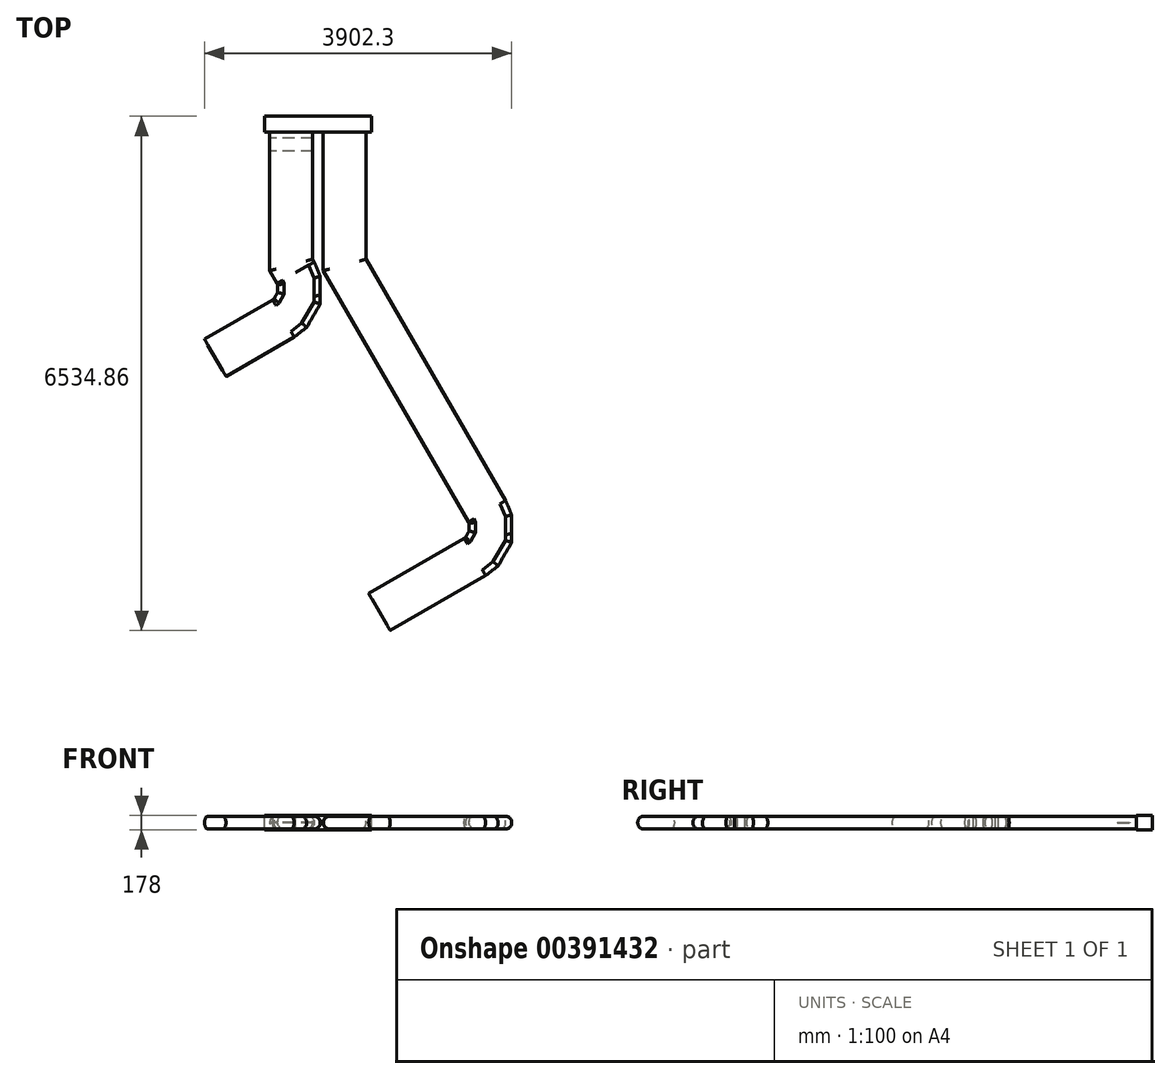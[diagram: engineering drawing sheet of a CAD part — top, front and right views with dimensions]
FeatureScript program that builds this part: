
annotation { "Feature Type Name" : "Feature", "Feature Type Description" : "" }
export const myFeature = defineFeature(function(context is Context, id is Id, definition is map)
    precondition{}
    {
        {
            var Q0;
            Q0=qCreatedBy(makeId("Front.planeOp"),FACE);
            var sketch = newSketch(context, id + "F0", { "sketchPlane" : qUnion([Q0])});
            skLineSegment(sketch, "E0.bottom", {"start": v(680, -89) * mm, "end": v(-680, -89) * mm});
            skLineSegment(sketch, "E0.top", {"start": v(680, 89) * mm, "end": v(-680, 89) * mm});
            skLineSegment(sketch, "E0.left", {"start": v(680, -89) * mm, "end": v(680, 89) * mm});
            skLineSegment(sketch, "E0.right", {"start": v(-680, -89) * mm, "end": v(-680, 89) * mm});
            skPoint(sketch, "E0.middle", {"position": v(0, 0) * mm});
            skSolve(sketch);
        }
        {
            var Q0;
            Q0=qSketchRegion(id+"F0",true);
            extrude(context, id + "F1", {"entities" : qUnion([Q0]), "depth" : 200 * mm});
        }
        {
            var Q0;
            Q0=makeQuery(id+"F1.opExtrude","CAP_FACE",FACE,{"disambiguationData":[OSD([sQuery(id+"F0.wireOp",EDGE,"E0.bottom"),sQuery(id+"F0.wireOp",EDGE,"E0.top"),sQuery(id+"F0.wireOp",EDGE,"E0.left"),sQuery(id+"F0.wireOp",EDGE,"E0.right")])],"isStart":false});
            var sketch = newSketch(context, id + "F2", { "sketchPlane" : qUnion([Q0])});
            skLineSegment(sketch, "E1.bottom", {"start": v(-150, -82.5) * mm, "end": v(-530, -82.5) * mm});
            skLineSegment(sketch, "E1.top", {"start": v(-150, 82.5) * mm, "end": v(-530, 82.5) * mm});
            skPoint(sketch, "E1.middle", {"position": v(-340, 0) * mm});
            skArc(sketch, "E2", {"start": v(-530, 82.5) * mm, "mid": v(-612.5, 0) * mm, "end": v(-530, -82.5) * mm});
            skArc(sketch, "E3", {"start": v(-150, -82.5) * mm, "mid": v(-67.5, 0) * mm, "end": v(-150, 82.5) * mm});
            skLineSegment(sketch, "E4.MirrorCS", {"start": v(150, -82.5) * mm, "end": v(530, -82.5) * mm});
            skLineSegment(sketch, "E5.MirrorCS", {"start": v(150, 82.5) * mm, "end": v(530, 82.5) * mm});
            skArc(sketch, "E6.MirrorCS", {"start": v(150, -82.5) * mm, "mid": v(67.5, 0) * mm, "end": v(150, 82.5) * mm});
            skArc(sketch, "E7.MirrorCS", {"start": v(530, 82.5) * mm, "mid": v(612.5, 0) * mm, "end": v(530, -82.5) * mm});
            skSolve(sketch);
        }
        {
            var Q0;
            Q0=makeQuery(id+"F2.imprint","IMPRINT",FACE,{"disambiguationData":[TD([[makeQuery(id+"F2.imprint","IMPRINT",EDGE,{"derivedFrom":sQuery(id+"F2.wireOp",EDGE,"E1.bottom")}),-1.0]])]});
            var Q1;
            Q1=makeQuery(id+"F2.imprint","IMPRINT",FACE,{"disambiguationData":[TD([[makeQuery(id+"F2.imprint","IMPRINT",EDGE,{"derivedFrom":sQuery(id+"F2.wireOp",EDGE,"E4.MirrorCS")}),1.0]])]});
            extrude(context, id + "F3", {"entities" : qUnion([Q0, Q1]), "operationType" : NewBodyOperationType.ADD, "depth" : 50 * mm});
        }
        {
            var Q0;
            Q0=makeQuery(id+"F1.opExtrude","SWEPT_BODY",BODY,{"disambiguationData":[OSD([sQuery(id+"F0.wireOp",EDGE,"E0.bottom"),sQuery(id+"F0.wireOp",EDGE,"E0.top"),sQuery(id+"F0.wireOp",EDGE,"E0.left"),sQuery(id+"F0.wireOp",EDGE,"E0.right")])]});
            transform(context, id + "F4", {"entities" : qUnion([Q0]), "transformType" : TransformType.TRANSLATION_3D, "dx" : 0 * mm, "dy" : 0 * mm, "dz" : 0 * mm, "makeCopy" : true});
        }
        {
            var Q0;
            Q0=makeQuery(id+"F4.opPattern","COPY",BODY,{"derivedFrom":makeQuery(id+"F1.opExtrude","SWEPT_BODY",BODY,{"disambiguationData":[OSD([sQuery(id+"F0.wireOp",EDGE,"E0.bottom"),sQuery(id+"F0.wireOp",EDGE,"E0.top"),sQuery(id+"F0.wireOp",EDGE,"E0.left"),sQuery(id+"F0.wireOp",EDGE,"E0.right")])]}),"instanceName":"1"});
            deleteBodies(context, id + "F5", {"entities" : qUnion([Q0])});
        }
        {
            var Q0;
            Q0=makeQuery(id+"F1.opExtrude","SWEPT_BODY",BODY,{"disambiguationData":[OSD([sQuery(id+"F0.wireOp",EDGE,"E0.bottom"),sQuery(id+"F0.wireOp",EDGE,"E0.top"),sQuery(id+"F0.wireOp",EDGE,"E0.left"),sQuery(id+"F0.wireOp",EDGE,"E0.right")])]});
            transform(context, id + "F6", {"entities" : qUnion([Q0]), "transformType" : TransformType.COPY});
        }
        {
            var Q0;
            Q0=makeQuery(id+"F6.opPattern","COPY",BODY,{"derivedFrom":makeQuery(id+"F1.opExtrude","SWEPT_BODY",BODY,{"disambiguationData":[OSD([sQuery(id+"F0.wireOp",EDGE,"E0.bottom"),sQuery(id+"F0.wireOp",EDGE,"E0.top"),sQuery(id+"F0.wireOp",EDGE,"E0.left"),sQuery(id+"F0.wireOp",EDGE,"E0.right")])]}),"instanceName":"1"});
            transform(context, id + "F7", {"entities" : qUnion([Q0]), "transformType" : TransformType.TRANSLATION_3D, "dx" : 0 * mm, "dy" : 0 * mm, "dz" : 0 * mm, "makeCopy" : true});
        }
        {
            var Q0;
            Q0=makeQuery(id+"F7.opPattern","COPY",BODY,{"derivedFrom":makeQuery(id+"F6.opPattern","COPY",BODY,{"derivedFrom":makeQuery(id+"F1.opExtrude","SWEPT_BODY",BODY,{"disambiguationData":[OSD([sQuery(id+"F0.wireOp",EDGE,"E0.bottom"),sQuery(id+"F0.wireOp",EDGE,"E0.top"),sQuery(id+"F0.wireOp",EDGE,"E0.left"),sQuery(id+"F0.wireOp",EDGE,"E0.right")])]}),"instanceName":"1"}),"instanceName":"1"});
            deleteBodies(context, id + "F8", {"entities" : qUnion([Q0])});
        }
        {
            var Q0;
            Q0=makeQuery(id+"F6.opPattern","COPY",BODY,{"derivedFrom":makeQuery(id+"F1.opExtrude","SWEPT_BODY",BODY,{"disambiguationData":[OSD([sQuery(id+"F0.wireOp",EDGE,"E0.bottom"),sQuery(id+"F0.wireOp",EDGE,"E0.top"),sQuery(id+"F0.wireOp",EDGE,"E0.left"),sQuery(id+"F0.wireOp",EDGE,"E0.right")])]}),"instanceName":"1"});
            deleteBodies(context, id + "F9", {"entities" : qUnion([Q0])});
        }
        {
            var Q0;
            Q0=makeQuery(id+"F3.opExtrude","CAP_FACE",FACE,{"disambiguationData":[OSD([sQuery(id+"F2.wireOp",EDGE,"E1.bottom"),sQuery(id+"F2.wireOp",EDGE,"E1.top"),sQuery(id+"F2.wireOp",EDGE,"E2"),sQuery(id+"F2.wireOp",EDGE,"E3")])],"isStart":false});
            var sketch = newSketch(context, id + "F10", { "sketchPlane" : qUnion([Q0])});
            skSolve(sketch);
        }
        {
            var Q0;
            Q0=makeQuery(id+"F10.imprint","IMPRINT",FACE,{"disambiguationData":[TD([[makeQuery(id+"F10.imprint","IMPRINT",EDGE,{"derivedFrom":makeQuery(id+"F3.opExtrude","CAP_EDGE",EDGE,{"disambiguationData":[OSD([sQuery(id+"F2.wireOp",EDGE,"E1.bottom")])],"isStart":false})}),-1.0]])]});
            extrude(context, id + "F11", {"entities" : qUnion([Q0]), "operationType" : NewBodyOperationType.ADD, "depth" : 25 * mm});
        }
        {
            var Q0;
            Q0=makeQuery(id+"F11.opExtrude","CAP_FACE",FACE,{"disambiguationData":[OSD([sQuery(id+"F2.wireOp",EDGE,"E1.bottom"),sQuery(id+"F2.wireOp",EDGE,"E1.top"),sQuery(id+"F2.wireOp",EDGE,"E2"),sQuery(id+"F2.wireOp",EDGE,"E3")])],"isStart":false});
            var sketch = newSketch(context, id + "F12", { "sketchPlane" : qUnion([Q0])});
            skLineSegment(sketch, "E8", {"start": v(-67.5, 0) * mm, "end": v(-612.5, 0) * mm, "construction": true});
            skLineSegment(sketch, "E9", {"start": v(-340, 82.5) * mm, "end": v(-340, -82.5) * mm, "construction": true});
            skLineSegment(sketch, "E10.bottom", {"start": v(-530, 82.5) * mm, "end": v(-150, 82.5) * mm});
            skLineSegment(sketch, "E10.top", {"start": v(-530, -82.5) * mm, "end": v(-150, -82.5) * mm});
            skPoint(sketch, "E10.middle", {"position": v(-340, 0) * mm});
            skArc(sketch, "E11", {"start": v(-530, 82.5) * mm, "mid": v(-587.98, 58.69) * mm, "end": v(-612.5, 1) * mm});
            skArc(sketch, "E12", {"start": v(-150, -82.5) * mm, "mid": v(-67.5, 0) * mm, "end": v(-150, 82.5) * mm});
            skLineSegment(sketch, "E13.0", {"start": v(-67.5, 1) * mm, "end": v(-612.5, 1) * mm});
            skLineSegment(sketch, "E14.0", {"start": v(-67.5, -1) * mm, "end": v(-612.5, -1) * mm});
            skArc(sketch, "E15.trimOffspring", {"start": v(-612.5, 0) * mm, "mid": v(-588.34, -58.34) * mm, "end": v(-530, -82.5) * mm});
            skSolve(sketch);
        }
        {
            var Q0;
            {var subQ0=sQuery(id+"F12.wireOp",EDGE,"E10.top");Q0=makeQuery(id+"F12.imprint","IMPRINT",FACE,{"disambiguationData":[TD([[makeQuery(id+"F12.imprint","IMPRINT",EDGE,{"derivedFrom":subQ0}),-1.0]])]});}
            var Q1;
            {var subQ0=sQuery(id+"F12.wireOp",EDGE,"E10.bottom");Q1=makeQuery(id+"F12.imprint","IMPRINT",FACE,{"disambiguationData":[TD([[makeQuery(id+"F12.imprint","IMPRINT",EDGE,{"derivedFrom":subQ0}),1.0]])]});}
            extrude(context, id + "F13", {"entities" : qUnion([Q0, Q1]), "operationType" : NewBodyOperationType.ADD, "depth" : 165 * mm});
        }
        {
            var Q0;
            Q0=makeQuery(id+"F3.opExtrude","CAP_FACE",FACE,{"disambiguationData":[OSD([sQuery(id+"F2.wireOp",EDGE,"E4.MirrorCS"),sQuery(id+"F2.wireOp",EDGE,"E5.MirrorCS"),sQuery(id+"F2.wireOp",EDGE,"E6.MirrorCS"),sQuery(id+"F2.wireOp",EDGE,"E7.MirrorCS")])],"isStart":false});
            extrude(context, id + "F14", {"entities" : qUnion([Q0]), "operationType" : NewBodyOperationType.ADD, "depth" : 1500 * mm});
        }
        {
            var Q0;
            Q0=makeQuery(id+"F13.opExtrude","CAP_FACE",FACE,{"disambiguationData":[OSD([sQuery(id+"F12.wireOp",EDGE,"E10.bottom"),sQuery(id+"F12.wireOp",EDGE,"E11"),sQuery(id+"F12.wireOp",EDGE,"E12"),sQuery(id+"F12.wireOp",EDGE,"E13.0")])],"isStart":false});
            var sketch = newSketch(context, id + "F15", { "sketchPlane" : qUnion([Q0])});
            skLineSegment(sketch, "E16", {"start": v(-340, 1) * mm, "end": v(-340, -1) * mm, "construction": true});
            skLineSegment(sketch, "E17.bottom", {"start": v(-150, -82.5) * mm, "end": v(-530, -82.5) * mm});
            skLineSegment(sketch, "E17.top", {"start": v(-150, 82.5) * mm, "end": v(-530, 82.5) * mm});
            skPoint(sketch, "E17.middle", {"position": v(-340, 0) * mm});
            skArc(sketch, "E18", {"start": v(-530, 82.5) * mm, "mid": v(-612.5, 0) * mm, "end": v(-530, -82.5) * mm});
            skArc(sketch, "E19", {"start": v(-150, -82.5) * mm, "mid": v(-67.5, 0) * mm, "end": v(-150, 82.5) * mm});
            skSolve(sketch);
        }
        {
            var Q0;
            Q0 = qSketchRegion(id + "F15", true);
            extrude(context, id + "F16", {"entities" : qUnion([Q0]), "operationType" : NewBodyOperationType.ADD, "depth" : 1335 * mm});
        }
        {
            var Q0;
            Q0=makeQuery(id+"F14.opExtrude","CAP_FACE",FACE,{"disambiguationData":[OSD([sQuery(id+"F2.wireOp",EDGE,"E4.MirrorCS"),sQuery(id+"F2.wireOp",EDGE,"E5.MirrorCS"),sQuery(id+"F2.wireOp",EDGE,"E6.MirrorCS"),sQuery(id+"F2.wireOp",EDGE,"E7.MirrorCS")])],"isStart":false});
            extrude(context, id + "F17", {"entities" : qUnion([Q0]), "operationType" : NewBodyOperationType.ADD, "depth" : 25 * mm});
        }
        {
            var Q0;
            Q0=makeQuery(id+"F16.opExtrude","CAP_FACE",FACE,{"disambiguationData":[OSD([sQuery(id+"F15.wireOp",EDGE,"E17.bottom"),sQuery(id+"F15.wireOp",EDGE,"E17.top"),sQuery(id+"F15.wireOp",EDGE,"E18"),sQuery(id+"F15.wireOp",EDGE,"E19")])],"isStart":false});
            var sketch = newSketch(context, id + "F18", { "sketchPlane" : qUnion([Q0])});
            skPoint(sketch, "E20", {"position": v(-340, 0) * mm});
            skPoint(sketch, "E21.orphan", {"position": v(-340, 82.5) * mm});
            skPoint(sketch, "E22.end.orphan", {"position": v(-340, -82.5) * mm});
            skPoint(sketch, "E23.orphan", {"position": v(-67.5, 0) * mm});
            skPoint(sketch, "E24.start.orphan", {"position": v(-612.5, 0) * mm});
            skLineSegment(sketch, "E25", {"start": v(-612.5, 0) * mm, "end": v(-67.5, 0) * mm, "construction": true});
            skLineSegment(sketch, "E26", {"start": v(-340, 82.5) * mm, "end": v(-340, -82.5) * mm, "construction": true});
            skSolve(sketch);
        }
        {
            var Q0;
            Q0=sQuery(id+"F18.wireOp",EDGE,"E25");
            cPlane(context, id + "F19", {"entities" : qUnion([Q0]), "cplaneType" : CPlaneType.LINE_ANGLE, "offset" : 25 * mm, "angle" : 90 * degree, "width" : 150 * mm, "height" : 150 * mm});
        }
        {
            var Q0;
            Q0=makeQuery(id+"F18.imprint","IMPRINT",FACE,{"disambiguationData":[TD([[makeQuery(id+"F18.imprint","IMPRINT",EDGE,{"derivedFrom":makeQuery(id+"F16.opExtrude","CAP_EDGE",EDGE,{"disambiguationData":[OSD([sQuery(id+"F15.wireOp",EDGE,"E17.bottom")])],"isStart":false})}),-1.0]])]});
            var sketch = newSketch(context, id + "F20", { "sketchPlane" : qUnion([Q0])});
            skArc(sketch, "E27.0", {"start": v(-530, 82.5) * mm, "mid": v(-612.5, 0) * mm, "end": v(-530, -82.5) * mm});
            skArc(sketch, "E27.1", {"start": v(-150, -82.5) * mm, "mid": v(-67.5, 0) * mm, "end": v(-150, 82.5) * mm});
            skLineSegment(sketch, "E28.0", {"start": v(-612.5, 0) * mm, "end": v(-67.5, 0) * mm, "construction": true});
            skLineSegment(sketch, "E28.1", {"start": v(-340, 82.5) * mm, "end": v(-340, -82.5) * mm, "construction": true});
            skPoint(sketch, "E29.0", {"position": v(-340, 0) * mm});
            skSolve(sketch);
        }
        {
            var Q0;
            Q0=qCreatedBy(id+"F19.planeOp",FACE);
            var sketch = newSketch(context, id + "F21", { "sketchPlane" : qUnion([Q0])});
            skPoint(sketch, "E30.0", {"position": v(-340, -1775) * mm});
            skPoint(sketch, "E31.0", {"position": v(-67.5, -1775) * mm});
            skPoint(sketch, "E32.0", {"position": v(-612.5, -1775) * mm});
            skLineSegment(sketch, "E33", {"start": v(-283.06, -1987.5) * mm, "end": v(85, -1775) * mm, "construction": true});
            skCircle(sketch, "E34", {"center": v(85, -1775) * mm, "radius": 425 * mm, "construction": true});
            skLineSegment(sketch, "E35", {"start": v(-340, -1775) * mm, "end": v(85, -1775) * mm, "construction": true});
            skLineSegment(sketch, "E36", {"start": v(-340, -1775) * mm, "end": v(-340, -1889) * mm});
            skLineSegment(sketch, "E37", {"start": v(-340, -1889) * mm, "end": v(-283.06, -1987.5) * mm});
            skSolve(sketch);
        }
        {
            var Q0;
            Q0=sQuery(id+"F21.wireOp",EDGE,"E33");
            cPlane(context, id + "F22", {"entities" : qUnion([Q0]), "cplaneType" : CPlaneType.LINE_ANGLE, "offset" : 25 * mm, "angle" : 0 * degree, "width" : 150 * mm, "height" : 150 * mm});
        }
        {
            var Q0;
            Q0=qCreatedBy(id+"F22.planeOp",FACE);
            var sketch = newSketch(context, id + "F23", { "sketchPlane" : qUnion([Q0])});
            skPoint(sketch, "E38.0", {"position": v(1238.89, 0) * mm});
            skLineSegment(sketch, "E39.bottom", {"start": v(1048.89, -82.5) * mm, "end": v(1428.89, -82.5) * mm});
            skLineSegment(sketch, "E39.top", {"start": v(1048.89, 82.5) * mm, "end": v(1428.89, 82.5) * mm});
            skArc(sketch, "E40", {"start": v(1428.89, -82.5) * mm, "mid": v(1511.39, 0) * mm, "end": v(1428.89, 82.5) * mm});
            skArc(sketch, "E41", {"start": v(1048.89, 82.5) * mm, "mid": v(966.39, 0) * mm, "end": v(1048.89, -82.5) * mm});
            skSolve(sketch);
        }
        {
            var Q0;
            Q0=makeQuery(id+"F17.opExtrude","CAP_FACE",FACE,{"disambiguationData":[OSD([sQuery(id+"F2.wireOp",EDGE,"E4.MirrorCS"),sQuery(id+"F2.wireOp",EDGE,"E5.MirrorCS"),sQuery(id+"F2.wireOp",EDGE,"E6.MirrorCS"),sQuery(id+"F2.wireOp",EDGE,"E7.MirrorCS")])],"isStart":false});
            var sketch = newSketch(context, id + "F24", { "sketchPlane" : qUnion([Q0])});
            skLineSegment(sketch, "E42", {"start": v(340, 82.5) * mm, "end": v(340, -82.5) * mm, "construction": true});
            skLineSegment(sketch, "E43", {"start": v(67.5, 0) * mm, "end": v(612.5, 0) * mm, "construction": true});
            skPoint(sketch, "E44", {"position": v(340, 0) * mm});
            skSolve(sketch);
        }
        {
            var Q0;
            Q0=sQuery(id+"F24.wireOp",EDGE,"E43");
            cPlane(context, id + "F25", {"entities" : qUnion([Q0]), "cplaneType" : CPlaneType.LINE_ANGLE, "offset" : 25 * mm, "angle" : 90 * degree, "width" : 150 * mm, "height" : 150 * mm});
        }
        {
            var Q0;
            Q0=qCreatedBy(id+"F25.planeOp",FACE);
            var sketch = newSketch(context, id + "F26", { "sketchPlane" : qUnion([Q0])});
            skPoint(sketch, "E45.0", {"position": v(340, -1775) * mm});
            skPoint(sketch, "E45.1", {"position": v(67.5, -1775) * mm});
            skPoint(sketch, "E45.2", {"position": v(612.5, -1775) * mm});
            skLineSegment(sketch, "E46", {"start": v(396.94, -1987.5) * mm, "end": v(765, -1775) * mm, "construction": true});
            skCircle(sketch, "E47", {"center": v(765, -1775) * mm, "radius": 425 * mm, "construction": true});
            skLineSegment(sketch, "E48", {"start": v(340, -1775) * mm, "end": v(340, -1889) * mm});
            skLineSegment(sketch, "E49", {"start": v(396.94, -1987.5) * mm, "end": v(340, -1889) * mm});
            skSolve(sketch);
        }
        {
            var Q0;
            Q0=makeQuery(id+"F18.imprint","IMPRINT",FACE,{"disambiguationData":[TD([[makeQuery(id+"F18.imprint","IMPRINT",EDGE,{"derivedFrom":makeQuery(id+"F16.opExtrude","CAP_EDGE",EDGE,{"disambiguationData":[OSD([sQuery(id+"F15.wireOp",EDGE,"E17.bottom")])],"isStart":false})}),-1.0]])]});
            var Q1;
            Q1=sQuery(id+"F21.wireOp",EDGE,"E36");
            var Q2;
            Q2=sQuery(id+"F21.wireOp",EDGE,"E37");
            sweep(context, id + "F27", {"operationType" : NewBodyOperationType.ADD, "profiles" : qUnion([Q0]), "path" : qUnion([Q1, Q2])});
        }
        {
            var Q0;
            Q0=makeQuery(id+"F24.imprint","IMPRINT",FACE,{"disambiguationData":[TD([[makeQuery(id+"F24.imprint","IMPRINT",EDGE,{"derivedFrom":makeQuery(id+"F17.opExtrude","CAP_EDGE",EDGE,{"disambiguationData":[OSD([sQuery(id+"F2.wireOp",EDGE,"E4.MirrorCS")])],"isStart":false})}),1.0]])]});
            var Q1;
            Q1=sQuery(id+"F26.wireOp",EDGE,"E48");
            var Q2;
            Q2=sQuery(id+"F26.wireOp",EDGE,"E49");
            sweep(context, id + "F28", {"operationType" : NewBodyOperationType.ADD, "profiles" : qUnion([Q0]), "path" : qUnion([Q1, Q2])});
        }
        {
            var Q0;
            Q0=makeQuery(id+"F23.imprint","IMPRINT",FACE,{"disambiguationData":[TD([[makeQuery(id+"F23.imprint","IMPRINT",EDGE,{"derivedFrom":sQuery(id+"F23.wireOp",EDGE,"E39.bottom")}),1.0]])]});
            var sketch = newSketch(context, id + "F29", { "sketchPlane" : qUnion([Q0])});
            skPoint(sketch, "E50.0", {"position": v(1238.89, 0) * mm});
            skPoint(sketch, "E50.1", {"position": v(1511.39, 0) * mm});
            skPoint(sketch, "E50.2", {"position": v(1238.89, 82.5) * mm});
            skPoint(sketch, "E50.3", {"position": v(1238.89, -82.5) * mm});
            skPoint(sketch, "E50.4", {"position": v(966.39, 0) * mm});
            skLineSegment(sketch, "E51", {"start": v(1511.39, 0) * mm, "end": v(966.39, 0) * mm, "construction": true});
            skLineSegment(sketch, "E52", {"start": v(1238.89, 82.5) * mm, "end": v(1238.89, -82.5) * mm, "construction": true});
            skSolve(sketch);
        }
        {
            var Q0;
            Q0=qCreatedBy(id+"F19.planeOp",FACE);
            var sketch = newSketch(context, id + "F30", { "sketchPlane" : qUnion([Q0])});
            skLineSegment(sketch, "E53.0", {"start": v(-519.05, -2123.75) * mm, "end": v(-47.07, -1851.25) * mm});
            skPoint(sketch, "E53.1", {"position": v(-519.05, -2123.75) * mm});
            skPoint(sketch, "E53.2", {"position": v(-47.07, -1851.25) * mm});
            skPoint(sketch, "E53.3", {"position": v(-283.06, -1987.5) * mm});
            skLineSegment(sketch, "E54", {"start": v(-283.06, -1987.5) * mm, "end": v(-651.12, -2200) * mm, "construction": true});
            skCircle(sketch, "E55", {"center": v(-651.12, -2200) * mm, "radius": 425 * mm, "construction": true});
            skLineSegment(sketch, "E56", {"start": v(-651.12, -2200) * mm, "end": v(-240.6, -2090) * mm, "construction": true});
            skPoint(sketch, "E57", {"position": v(-350.6, -2500.52) * mm});
            skPoint(sketch, "E58", {"position": v(-240.6, -2310) * mm});
            skPoint(sketch, "E59", {"position": v(-240.6, -2090) * mm});
            skLineSegment(sketch, "E60", {"start": v(-651.12, -2200) * mm, "end": v(-438.62, -2568.06) * mm, "construction": true});
            skLineSegment(sketch, "E61", {"start": v(-283.06, -1987.5) * mm, "end": v(-240.6, -2090) * mm});
            skLineSegment(sketch, "E62", {"start": v(-240.6, -2090) * mm, "end": v(-240.6, -2310) * mm});
            skLineSegment(sketch, "E63", {"start": v(-240.6, -2310) * mm, "end": v(-350.6, -2500.52) * mm});
            skLineSegment(sketch, "E64", {"start": v(-350.6, -2500.52) * mm, "end": v(-438.62, -2568.06) * mm});
            skSolve(sketch);
        }
        {
            var Q0;
            Q0=makeQuery(id+"F28.opSweep","CAP_FACE",FACE,{"disambiguationData":[OSD([sQuery(id+"F2.wireOp",EDGE,"E4.MirrorCS"),sQuery(id+"F2.wireOp",EDGE,"E5.MirrorCS"),sQuery(id+"F2.wireOp",EDGE,"E6.MirrorCS"),sQuery(id+"F2.wireOp",EDGE,"E7.MirrorCS"),sQuery(id+"F26.wireOp",VERTEX,"E49.start")])],"isStart":false});
            extrude(context, id + "F31", {"entities" : qUnion([Q0]), "operationType" : NewBodyOperationType.ADD, "depth" : 3500 * mm});
        }
        {
            var Q0;
            Q0=makeQuery(id+"F31.opExtrude","CAP_FACE",FACE,{"disambiguationData":[OSD([sQuery(id+"F2.wireOp",EDGE,"E4.MirrorCS"),sQuery(id+"F2.wireOp",EDGE,"E5.MirrorCS"),sQuery(id+"F2.wireOp",EDGE,"E6.MirrorCS"),sQuery(id+"F2.wireOp",EDGE,"E7.MirrorCS"),sQuery(id+"F26.wireOp",VERTEX,"E49.start")])],"isStart":false});
            var sketch = newSketch(context, id + "F32", { "sketchPlane" : qUnion([Q0])});
            skPoint(sketch, "E65.0", {"position": v(-923.52, 0) * mm});
            skPoint(sketch, "E65.1", {"position": v(-651.02, 82.5) * mm});
            skPoint(sketch, "E65.2", {"position": v(-651.02, -82.5) * mm});
            skPoint(sketch, "E65.3", {"position": v(-378.52, 0) * mm});
            skLineSegment(sketch, "E66", {"start": v(-923.52, 0) * mm, "end": v(-378.52, 0) * mm, "construction": true});
            skLineSegment(sketch, "E67", {"start": v(-651.02, -82.5) * mm, "end": v(-651.02, 82.5) * mm, "construction": true});
            skPoint(sketch, "E68", {"position": v(-651.02, 0) * mm});
            skSolve(sketch);
        }
        {
            var Q0;
            Q0=sQuery(id+"F32.wireOp",EDGE,"E66");
            cPlane(context, id + "F33", {"entities" : qUnion([Q0]), "cplaneType" : CPlaneType.LINE_ANGLE, "offset" : 25 * mm, "angle" : 90 * degree, "width" : 150 * mm, "height" : 150 * mm});
        }
        {
            var Q0;
            Q0=qCreatedBy(id+"F33.planeOp",FACE);
            var sketch = newSketch(context, id + "F34", { "sketchPlane" : qUnion([Q0])});
            skPoint(sketch, "E69.0", {"position": v(1912.64, -5154.03) * mm});
            skLineSegment(sketch, "E69.1", {"start": v(1912.64, -5154.03) * mm, "end": v(2384.48, -4881.28) * mm});
            skPoint(sketch, "E69.2", {"position": v(2148.56, -5017.65) * mm});
            skPoint(sketch, "E69.3", {"position": v(2384.48, -4881.28) * mm});
            skLineSegment(sketch, "E70", {"start": v(2148.56, -5017.65) * mm, "end": v(1780.61, -5230.35) * mm, "construction": true});
            skCircle(sketch, "E71", {"center": v(1780.61, -5230.35) * mm, "radius": 425 * mm, "construction": true});
            skLineSegment(sketch, "E72", {"start": v(1780.61, -5230.35) * mm, "end": v(2081.3, -5530.7) * mm, "construction": true});
            skLineSegment(sketch, "E73", {"start": v(1780.61, -5230.35) * mm, "end": v(2191.07, -5120.13) * mm, "construction": true});
            skPoint(sketch, "E74", {"position": v(2081.3, -5530.7) * mm});
            skPoint(sketch, "E75", {"position": v(2191.19, -5340.13) * mm});
            skLineSegment(sketch, "E76", {"start": v(1780.61, -5230.35) * mm, "end": v(1993.3, -5598.3) * mm, "construction": true});
            skPoint(sketch, "E77", {"position": v(2191.07, -5120.13) * mm});
            skLineSegment(sketch, "E78", {"start": v(2148.56, -5017.65) * mm, "end": v(2191.07, -5120.13) * mm});
            skLineSegment(sketch, "E79", {"start": v(2191.07, -5120.13) * mm, "end": v(2191.19, -5340.13) * mm});
            skLineSegment(sketch, "E80", {"start": v(2191.19, -5340.13) * mm, "end": v(2081.3, -5530.7) * mm});
            skLineSegment(sketch, "E81", {"start": v(2081.3, -5530.7) * mm, "end": v(1993.3, -5598.3) * mm});
            skSolve(sketch);
        }
        {
            var Q0;
            Q0=sQuery(id+"F34.wireOp",EDGE,"E76");
            cPlane(context, id + "F35", {"entities" : qUnion([Q0]), "cplaneType" : CPlaneType.LINE_ANGLE, "offset" : 25 * mm, "angle" : 90 * degree, "width" : 150 * mm, "height" : 150 * mm});
        }
        {
            var Q0;
            Q0=qCreatedBy(id+"F35.planeOp",FACE);
            var sketch = newSketch(context, id + "F36", { "sketchPlane" : qUnion([Q0])});
            skPoint(sketch, "E82.0", {"position": v(-5844.35, 0) * mm});
            skLineSegment(sketch, "E83.bottom", {"start": v(-6034.35, -82.5) * mm, "end": v(-5654.35, -82.5) * mm});
            skLineSegment(sketch, "E83.top", {"start": v(-6034.35, 82.5) * mm, "end": v(-5654.35, 82.5) * mm});
            skArc(sketch, "E84", {"start": v(-5654.35, -82.5) * mm, "mid": v(-5571.85, 0) * mm, "end": v(-5654.35, 82.5) * mm});
            skArc(sketch, "E85", {"start": v(-6034.35, 82.5) * mm, "mid": v(-6116.85, 0) * mm, "end": v(-6034.35, -82.5) * mm});
            skSolve(sketch);
        }
        {
            var Q0;
            {var subQ0=sQuery(id+"F26.wireOp",VERTEX,"E49.start");Q0=makeQuery(id+"F32.imprint","IMPRINT",FACE,{"disambiguationData":[TD([[makeQuery(id+"F32.imprint","IMPRINT",EDGE,{"derivedFrom":makeQuery(id+"F31.opExtrude","CAP_EDGE",EDGE,{"disambiguationData":[OSD([sQuery(id+"F2.wireOp",EDGE,"E4.MirrorCS"),subQ0])],"isStart":false})}),1.0]])]});}
            var Q1;
            Q1=sQuery(id+"F34.wireOp",EDGE,"E78");
            var Q2;
            Q2=sQuery(id+"F34.wireOp",EDGE,"E79");
            sweep(context, id + "F37", {"operationType" : NewBodyOperationType.ADD, "profiles" : qUnion([Q0]), "path" : qUnion([Q1, Q2])});
        }
        {
            var Q0;
            Q0=makeQuery(id+"F36.imprint","IMPRINT",FACE,{"disambiguationData":[TD([[makeQuery(id+"F36.imprint","IMPRINT",EDGE,{"derivedFrom":sQuery(id+"F36.wireOp",EDGE,"E83.bottom")}),1.0]])]});
            var Q1;
            Q1=sQuery(id+"F34.wireOp",EDGE,"E81");
            var Q2;
            Q2=sQuery(id+"F34.wireOp",EDGE,"E80");
            var Q3;
            Q3=sQuery(id+"F34.wireOp",EDGE,"E79");
            sweep(context, id + "F38", {"operationType" : NewBodyOperationType.ADD, "profiles" : qUnion([Q0]), "path" : qUnion([Q1, Q2, Q3])});
        }
        {
            var Q0;
            Q0=makeQuery(id+"F38.opSweep","CAP_FACE",FACE,{"disambiguationData":[OSD([sQuery(id+"F34.wireOp",VERTEX,"E81.end"),sQuery(id+"F36.wireOp",EDGE,"E83.bottom"),sQuery(id+"F36.wireOp",EDGE,"E83.top"),sQuery(id+"F36.wireOp",EDGE,"E84"),sQuery(id+"F36.wireOp",EDGE,"E85")])],"isStart":true});
            extrude(context, id + "F39", {"entities" : qUnion([Q0]), "operationType" : NewBodyOperationType.ADD, "depth" : 1400 * mm});
        }
        {
            var Q0;
            Q0=sQuery(id+"F30.wireOp",EDGE,"E60");
            cPlane(context, id + "F40", {"entities" : qUnion([Q0]), "cplaneType" : CPlaneType.LINE_ANGLE, "offset" : 25 * mm, "angle" : 90 * degree, "width" : 150 * mm, "height" : 150 * mm});
        }
        {
            var Q0;
            Q0=qCreatedBy(id+"F40.planeOp",FACE);
            var sketch = newSketch(context, id + "F41", { "sketchPlane" : qUnion([Q0])});
            skPoint(sketch, "E86.0", {"position": v(-2004.7, 0) * mm});
            skLineSegment(sketch, "E87.bottom", {"start": v(-2194.7, -82.5) * mm, "end": v(-1814.7, -82.5) * mm});
            skLineSegment(sketch, "E87.top", {"start": v(-2194.7, 82.5) * mm, "end": v(-1814.7, 82.5) * mm});
            skArc(sketch, "E88", {"start": v(-1814.7, -82.5) * mm, "mid": v(-1732.2, 0) * mm, "end": v(-1814.7, 82.5) * mm});
            skArc(sketch, "E89", {"start": v(-2194.7, 82.5) * mm, "mid": v(-2277.2, 0) * mm, "end": v(-2194.7, -82.5) * mm});
            skSolve(sketch);
        }
        {
            var Q0;
            Q0=makeQuery(id+"F29.imprint","IMPRINT",FACE,{"disambiguationData":[TD([[makeQuery(id+"F29.imprint","IMPRINT",EDGE,{"derivedFrom":makeQuery(id+"F23.imprint","IMPRINT",EDGE,{"derivedFrom":sQuery(id+"F23.wireOp",EDGE,"E39.bottom")})}),1.0]])]});
            var Q1;
            Q1=sQuery(id+"F30.wireOp",EDGE,"E61");
            var Q2;
            Q2=sQuery(id+"F30.wireOp",EDGE,"E62");
            sweep(context, id + "F42", {"profiles" : qUnion([Q0]), "path" : qUnion([Q1, Q2])});
        }
        {
            var Q0;
            Q0=makeQuery(id+"F41.imprint","IMPRINT",FACE,{"disambiguationData":[TD([[makeQuery(id+"F41.imprint","IMPRINT",EDGE,{"derivedFrom":sQuery(id+"F41.wireOp",EDGE,"E87.bottom")}),1.0]])]});
            var Q1;
            Q1=sQuery(id+"F30.wireOp",EDGE,"E64");
            var Q2;
            Q2=sQuery(id+"F30.wireOp",EDGE,"E63");
            var Q3;
            Q3=sQuery(id+"F30.wireOp",EDGE,"E62");
            sweep(context, id + "F43", {"operationType" : NewBodyOperationType.ADD, "profiles" : qUnion([Q0]), "path" : qUnion([Q1, Q2, Q3])});
        }
        {
            var Q0;
            Q0=makeQuery(id+"F43.opSweep","CAP_FACE",FACE,{"disambiguationData":[OSD([sQuery(id+"F30.wireOp",VERTEX,"E64.end"),sQuery(id+"F41.wireOp",EDGE,"E87.bottom"),sQuery(id+"F41.wireOp",EDGE,"E87.top"),sQuery(id+"F41.wireOp",EDGE,"E88"),sQuery(id+"F41.wireOp",EDGE,"E89")])],"isStart":true});
            extrude(context, id + "F44", {"entities" : qUnion([Q0]), "operationType" : NewBodyOperationType.ADD, "depth" : 1000 * mm});
        }
    });
